# Revit family: IEK_РозеткаСетевая_ОткрытойУстановки_C ЗК с КР 16А четырехместная IP54_ГЕРМЕС PLUS
name_source: partatom
category: Электрические приборы
units: mm (PartAtom-declared; Revit-internal decimal feet)

## family parameters
Всегда вертикально = Да
На основе рабочей плоскости = Нет
Общий = Нет
При загрузке вырезать с полостями = Нет
Размер круглого соединителя = Использовать диаметр
Сохранять ориентацию аннотаций = Да
Тип детали = Нормальный
Точка расчета площади = Нет

## types (2) — shared parameters
ADSK_URL страницы изделия = https://www.iek.ru
ADSK_Версия Revit = 2019
ADSK_Версия семейства = 1.0
ADSK_Группирование = III ЭЛЕКТРОУСТАНОВОЧНЫЕ И ЭЛЕКТРОМОНТАЖНЫЕ ИЗДЕЛИЯ
ADSK_Единица измерения = шт
ADSK_Завод-изготовитель = IEK
ADSK_Количество фаз = 1
ADSK_Количество фаз числовое = 1
ADSK_Марка = ГЕРМЕС PLUS
ADSK_Масса = 0.513
ADSK_Материал = Цвет белый
ADSK_Материал наименование = Пластик
ADSK_Напряжение = 220 В
IEK_URL = https://www.iek.ru
IEK_Описание = Изделия серии "ГЕРМЕС PLUS" используются в помещениях с повышенной влажностью или запыленностью, а также под навесом на открытом воздухе.
IEK_Цена за единицу = 1217.23
KSI_CMa_Строительные материалы = 01.7.14.03
KSI_CPr_Строительные изделия = 20.4.03.04 20.4.03.05 20.4.03.06
Высота = 72 мм
Глубина = 52 мм
Изготовитель = IEK
Степень защиты = IP54
Тип монтажа = Поверхность монтажа (открытая установка)
Ширина = 290 мм

## per-type parameters (varying)
| type | ADSK_Код изделия | ADSK_Наименование | Материал крышки |
| РСб24-3-ГПБб | ERMP42-K01-16-54-EC | Розетка 4-местная для открытой установки РСб24-3-ГПБб с заземляющим контактом IP54 ГЕРМЕС PLUS белый IEK | Цвет белый |
| РСб24-3-ГПБд | ERMP42-K03-16-54-EC | Розетка 4-местная для открытой установки РСб24-3-ГПБд с заземляющим контактом IP54 ГЕРМЕС PLUS (цвет крышки: дымчатый) IEK | Цвет дымчатый |
